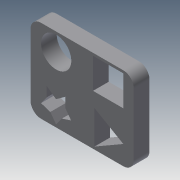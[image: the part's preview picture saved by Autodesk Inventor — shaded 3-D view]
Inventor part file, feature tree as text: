
AUTODESK INVENTOR PART (.ipt)
format: ipt  version: 2015 (Build 190159000, 159)  size: 120,320 bytes
history: native  units: in
note: dims shown in document units (in); Inventor stores cm internally (conversion verified against a paired STEP export)
features: extrude x1, sketch x1
ambient origin geometry x8: Origin, YZ Plane, XZ Plane, XY Plane, X Axis, Y Axis, Z Axis, Center Point
bodies: Solid1 (feature_tree)
feature tree (2):
  extrude  "Extrusion1"  Depth=1.59in
  sketch  "Sketch1"  dims[d0=1.975in d1=1.59in d2=0.2in d3=0.58in d4=0.49in d5=0.34in d6=0.58in d7=0.58in d8=0.05in d9=0.2in d20=0.638in d21=0.05in d22=0.2in d23=0.187in d24=0.187in d25=0.0935in d26=0.488in d27=0.05in d28=0.3in d29=0.0in]
